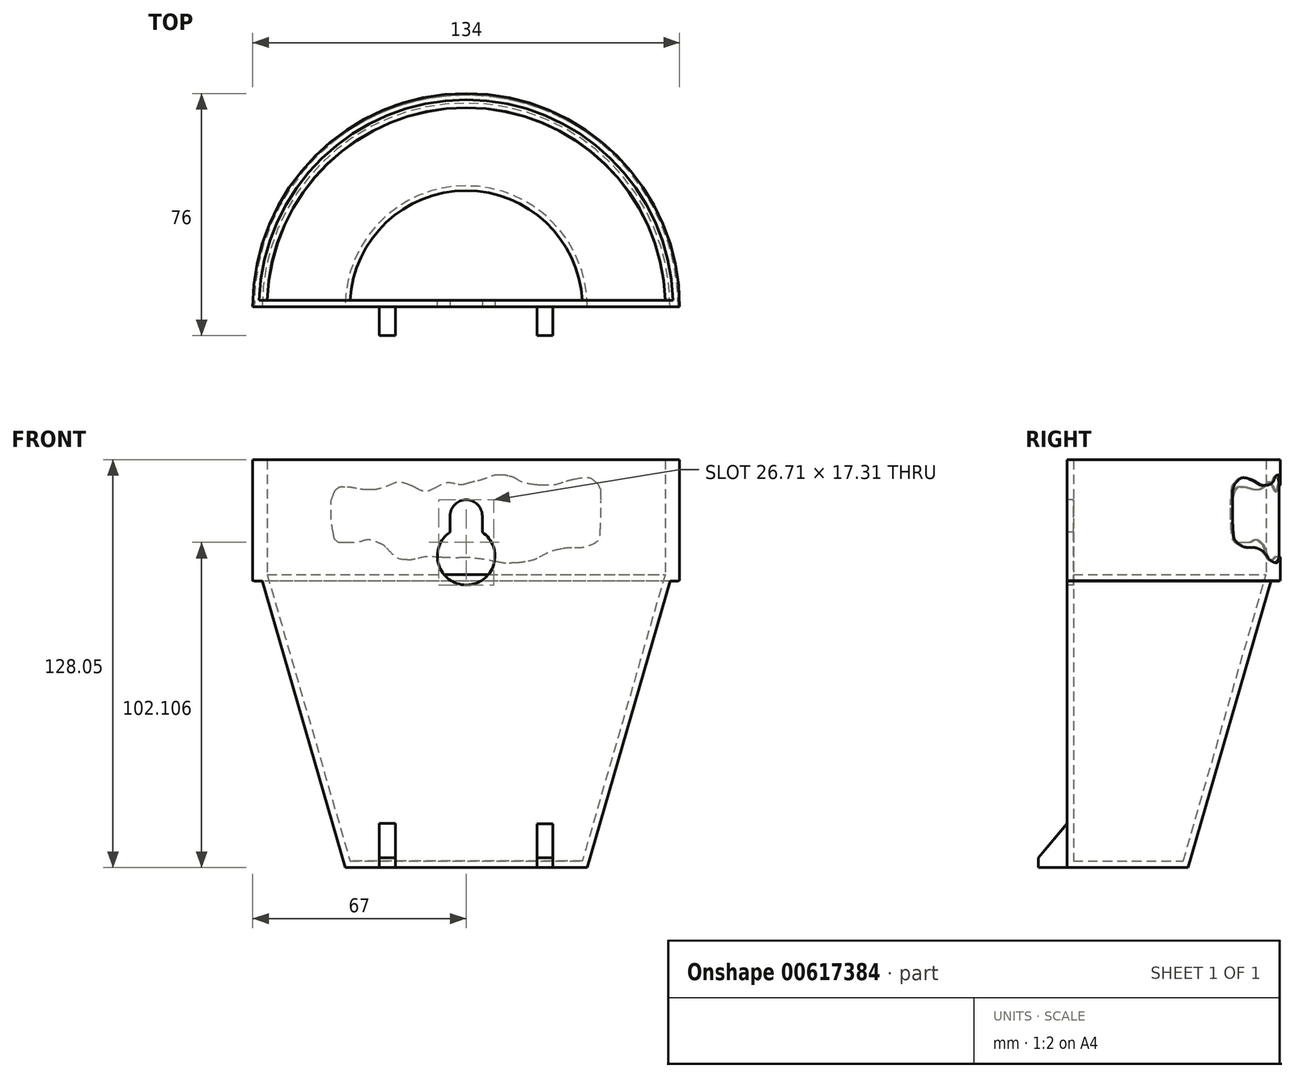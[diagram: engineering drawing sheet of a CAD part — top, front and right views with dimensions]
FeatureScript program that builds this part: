
annotation { "Feature Type Name" : "Feature", "Feature Type Description" : "" }
export const myFeature = defineFeature(function(context is Context, id is Id, definition is map)
    precondition{}
    {
        {
            var Q0;
            Q0=qCreatedBy(makeId("Front.planeOp"),FACE);
            var sketch = newSketch(context, id + "F0", { "sketchPlane" : qUnion([Q0])});
            skLineSegment(sketch, "E0", {"start": v(0, 56.42) * mm, "end": v(-67, 56.42) * mm});
            skLineSegment(sketch, "E1", {"start": v(-67, 56.42) * mm, "end": v(-67, 18.42) * mm});
            skLineSegment(sketch, "E2", {"start": v(0, -71.58) * mm, "end": v(-38, -71.58) * mm});
            skLineSegment(sketch, "E3", {"start": v(-67, 18.42) * mm, "end": v(-64, 18.42) * mm});
            skLineSegment(sketch, "E4", {"start": v(0, 56.42) * mm, "end": v(0, -71.58) * mm});
            skLineSegment(sketch, "E5", {"start": v(-64, 18.42) * mm, "end": v(-38, -71.58) * mm});
            skLineSegment(sketch, "E6.MirrorCS", {"start": v(0, 56.42) * mm, "end": v(67, 56.42) * mm});
            skLineSegment(sketch, "E7.MirrorCS", {"start": v(67, 56.42) * mm, "end": v(67, 18.42) * mm});
            skLineSegment(sketch, "E8.MirrorCS", {"start": v(67, 18.42) * mm, "end": v(64, 18.42) * mm});
            skLineSegment(sketch, "E9.MirrorCS", {"start": v(64, 18.42) * mm, "end": v(38, -71.58) * mm});
            skLineSegment(sketch, "E10.MirrorCS", {"start": v(0, -71.58) * mm, "end": v(38, -71.58) * mm});
            skSolve(sketch);
        }
        {
            var Q0;
            {var subQ0=sQuery(id+"F0.wireOp",EDGE,"E3");Q0=makeQuery(id+"F0.imprint","IMPRINT",FACE,{"disambiguationData":[TD([[makeQuery(id+"F0.imprint","IMPRINT",EDGE,{"derivedFrom":subQ0}),1.0]])]});}
            var Q1;
            {var subQ1=sQuery(id+"F0.wireOp",EDGE,"E0");Q1=makeQuery(id+"F0.imprint","IMPRINT",FACE,{"disambiguationData":[TD([[makeQuery(id+"F0.imprint","IMPRINT",EDGE,{"derivedFrom":subQ1}),1.0]])]});}
            var Q2;
            Q2=makeQuery(id+"F0.imprint","IMPRINT",FACE,{"disambiguationData":[TD([[makeQuery(id+"F0.imprint","IMPRINT",EDGE,{"derivedFrom":sQuery(id+"F0.wireOp",EDGE,"Kfnrekvc-ZjTY-c2iQ-cK4z-hKnBe4uEAVNk")}),1.0]])]});
            var Q3;
            Q3=sQuery(id+"F0.wireOp",EDGE,"E4");
            revolve(context, id + "F1", {"entities" : qUnion([Q0, Q1, Q2]), "axis" : qUnion([Q3]), "revolveType" : RevolveType.ONE_DIRECTION, "angle" : 180 * degree});
        }
        {
            var Q0;
            Q0=makeQuery(id+"FK2OT3XlAi37Aaq_1.splitOp","SPLIT",FACE,{"derivedFrom":makeQuery(id+"F1.opRevolve","SWEPT_FACE",FACE,{"disambiguationData":[OSD([sQuery(id+"F0.wireOp",EDGE,"E0")])]}),"isFromBackBody":true});
            shell(context, id + "F2", {"entities" : qUnion([Q0]), "thickness" : 2 * mm});
        }
        {
            var Q0;
            Q0=qCreatedBy(makeId("Front.planeOp"),FACE);
            var sketch = newSketch(context, id + "F3", { "sketchPlane" : qUnion([Q0])});
            skPoint(sketch, "E11.middle", {"position": v(0, -64.08) * mm});
            skLineSegment(sketch, "E12.bottom", {"start": v(-27.21, -56.57) * mm, "end": v(-22.21, -56.57) * mm});
            skLineSegment(sketch, "E12.top", {"start": v(-27.21, -71.57) * mm, "end": v(-22.21, -71.57) * mm});
            skLineSegment(sketch, "E12.left", {"start": v(-27.21, -56.57) * mm, "end": v(-27.21, -71.57) * mm});
            skLineSegment(sketch, "E12.right", {"start": v(-22.21, -56.57) * mm, "end": v(-22.21, -71.57) * mm});
            skPoint(sketch, "E12.middle", {"position": v(-24.71, -64.07) * mm});
            skLineSegment(sketch, "E13.bottom", {"start": v(22.21, -56.63) * mm, "end": v(27.21, -56.63) * mm});
            skLineSegment(sketch, "E13.top", {"start": v(22.21, -71.63) * mm, "end": v(27.21, -71.63) * mm});
            skLineSegment(sketch, "E13.left", {"start": v(22.21, -56.63) * mm, "end": v(22.21, -71.63) * mm});
            skLineSegment(sketch, "E13.right", {"start": v(27.21, -56.63) * mm, "end": v(27.21, -71.63) * mm});
            skPoint(sketch, "E13.middle", {"position": v(24.71, -64.13) * mm});
            skLineSegment(sketch, "E14", {"start": v(0, -71.68) * mm, "end": v(-22.21, -71.57) * mm, "construction": true});
            skLineSegment(sketch, "E15", {"start": v(0, -71.68) * mm, "end": v(22.21, -71.63) * mm, "construction": true});
            skSolve(sketch);
        }
        {
            var Q0;
            Q0=qSketchRegion(id+"F3",true);
            extrude(context, id + "F4", {"entities" : qUnion([Q0]), "operationType" : NewBodyOperationType.ADD, "depth" : 9 * mm});
        }
        {
            var Q0;
            Q0=qCreatedBy(makeId("Front.planeOp"),FACE);
            var sketch = newSketch(context, id + "F5", { "sketchPlane" : qUnion([Q0])});
            skCircle(sketch, "E16", {"center": v(0, 26.17) * mm, "radius": 9.05 * mm});
            skArc(sketch, "E17", {"start": v(5.05, 38.78) * mm, "mid": v(0.02, 43.83) * mm, "end": v(-5.05, 38.81) * mm});
            skLineSegment(sketch, "E18", {"start": v(-5.05, 38.81) * mm, "end": v(-5.05, 33.68) * mm});
            skLineSegment(sketch, "E19", {"start": v(5.05, 38.78) * mm, "end": v(5.05, 33.68) * mm});
            skSolve(sketch);
        }
        {
            var Q0;
            {var subQ0=sQuery(id+"F5.wireOp",EDGE,"E16");var subQ1=sQuery(id+"F5.wireOp",EDGE,"mXHq6PA0-CqQh-Lv1D-GdnR-uttjTBgCqYAd");var subQ2=makeQuery(id+"F5.imprint","INTERSECT",VERTEX,{"disambiguationData":[OD(0.0)],"derivedFrom":[subQ1,subQ0]});Q0=makeQuery(id+"F5.imprint","IMPRINT",FACE,{"disambiguationData":[TD([[makeQuery(id+"F5.imprint","IMPRINT",EDGE,{"disambiguationData":[TD([[subQ2,1.0]])],"derivedFrom":subQ1}),1.0]])]});}
            var Q1;
            {var subQ0=sQuery(id+"F5.wireOp",EDGE,"E16");var subQ1=sQuery(id+"F5.wireOp",EDGE,"mXHq6PA0-CqQh-Lv1D-GdnR-uttjTBgCqYAd");var subQ2=makeQuery(id+"F5.imprint","INTERSECT",VERTEX,{"disambiguationData":[OD(0.0)],"derivedFrom":[subQ1,subQ0]});Q1=makeQuery(id+"F5.imprint","IMPRINT",FACE,{"disambiguationData":[TD([[makeQuery(id+"F5.imprint","IMPRINT",EDGE,{"disambiguationData":[TD([[subQ2,-1.0]])],"derivedFrom":subQ1}),-1.0]])]});}
            var Q2;
            {var subQ0=sQuery(id+"F5.wireOp",EDGE,"E16");var subQ1=sQuery(id+"F5.wireOp",EDGE,"mXHq6PA0-CqQh-Lv1D-GdnR-uttjTBgCqYAd");var subQ2=makeQuery(id+"F5.imprint","INTERSECT",VERTEX,{"disambiguationData":[OD(0.0)],"derivedFrom":[subQ1,subQ0]});Q2=makeQuery(id+"F5.imprint","IMPRINT",FACE,{"disambiguationData":[TD([[makeQuery(id+"F5.imprint","IMPRINT",EDGE,{"disambiguationData":[TD([[subQ2,-1.0]])],"derivedFrom":subQ1}),1.0]])]});}
            var Q3;
            Q3=makeQuery(id+"F5.imprint","IMPRINT",FACE,{"disambiguationData":[TD([[makeQuery(id+"F5.imprint","IMPRINT",EDGE,{"derivedFrom":sQuery(id+"F5.wireOp",EDGE,"E17")}),1.0]])]});
            var Q4;
            {var subQ0=sQuery(id+"F5.wireOp",EDGE,"E16");var subQ1=makeQuery(id+"F5.imprint","INTERSECT",VERTEX,{"derivedFrom":[subQ0,sQuery(id+"F5.wireOp",EDGE,"E18")]});Q4=makeQuery(id+"F5.imprint","IMPRINT",FACE,{"disambiguationData":[TD([[makeQuery(id+"F5.imprint","IMPRINT",EDGE,{"disambiguationData":[TD([[subQ1,1.0]])],"derivedFrom":subQ0}),1.0]])]});}
            var Q5;
            Q5=sQuery(id+"F5.wireOp",EDGE,"mXHq6PA0-CqQh-Lv1D-GdnR-uttjTBgCqYAd");
            var Q6;
            Q6=sQuery(id+"F5.wireOp",EDGE,"E16");
            extrude(context, id + "F6", {"entities" : qUnion([Q0, Q1, Q2, Q3, Q4]), "operationType" : NewBodyOperationType.REMOVE, "surfaceEntities" : qUnion([Q5, Q6]), "oppositeDirection" : true, "depth" : 10 * mm, "offsetDistance" : 25 * mm});
        }
        {
            var Q0;
            Q0=makeQuery(id+"F4.opExtrude","CAP_EDGE",EDGE,{"disambiguationData":[OSD([sQuery(id+"F3.wireOp",EDGE,"E11.bottom")])],"isStart":false});
            var Q1;
            Q1=makeQuery(id+"F4.opExtrude","CAP_EDGE",EDGE,{"disambiguationData":[OSD([sQuery(id+"F3.wireOp",EDGE,"E12.bottom")])],"isStart":false});
            var Q2;
            Q2=makeQuery(id+"F4.opExtrude","CAP_EDGE",EDGE,{"disambiguationData":[OSD([sQuery(id+"F3.wireOp",EDGE,"E13.bottom")])],"isStart":false});
            chamfer(context, id + "F7", {"entities" : qUnion([Q0, Q1, Q2]), "chamferType" : ChamferType.OFFSET_ANGLE, "width" : 10 * mm, "oppositeDirection" : false, "angle" : 50 * degree, "tangentPropagation" : true});
        }
        {
            var Q0;
            Q0=makeQuery(id+"F2.opShell","OFFSET_FACE",FACE,{"disambiguationData":[OSD([sQuery(id+"F0.wireOp",EDGE,"E0"),sQuery(id+"F0.wireOp",EDGE,"E1"),sQuery(id+"F0.wireOp",EDGE,"E2"),sQuery(id+"F0.wireOp",EDGE,"E3"),sQuery(id+"F0.wireOp",EDGE,"E4"),sQuery(id+"F0.wireOp",EDGE,"E5")])]});
            cPlane(context, id + "F8", {"entities" : qUnion([Q0]), "cplaneType" : CPlaneType.OFFSET, "offset" : 66.8 * mm, "width" : 150 * mm, "height" : 150 * mm});
        }
        {
            var Q0;
            Q0=makeQuery(id+"F1.opRevolve","SWEPT_FACE",FACE,{"disambiguationData":[OSD([sQuery(id+"F0.wireOp",EDGE,"E0")])]});
            var sketch = newSketch(context, id + "F9", { "sketchPlane" : qUnion([Q0])});
            skCircle(sketch, "E20", {"center": v(0, 0) * mm, "radius": 67.75 * mm});
            skCircle(sketch, "E21", {"center": v(0, 0) * mm, "radius": 91 * mm});
            skSolve(sketch);
        }
        {
            var Q0;
            Q0=qSketchRegion(id+"F9",true);
            extrude(context, id + "F10", {"entities" : qUnion([Q0]), "operationType" : NewBodyOperationType.REMOVE, "oppositeDirection" : true, "depth" : 124 * mm});
        }
        {
            var Q0;
            Q0=qCreatedBy(id+"F8.planeOp",FACE);
            var sketch = newSketch(context, id + "F11", { "sketchPlane" : qUnion([Q0])});
            skFitSpline(sketch, "E22", {"points": [v(-14.21, 60.71) * mm, v(-15.23, 60.8) * mm, v(-17.15, 61.07) * mm, v(-17.98, 61.24) * mm]});
            skFitSpline(sketch, "E23", {"points": [v(-17.98, 61.24) * mm, v(-19.27, 61.5) * mm, v(-20.2, 61.84) * mm, v(-21.41, 62.47) * mm]});
            skFitSpline(sketch, "E24", {"points": [v(-21.41, 62.47) * mm, v(-24.2, 63.93) * mm, v(-26.13, 64.66) * mm, v(-28.48, 65.15) * mm]});
            skFitSpline(sketch, "E25", {"points": [v(-28.48, 65.15) * mm, v(-29.29, 65.32) * mm, v(-30, 65.37) * mm, v(-32.2, 65.43) * mm]});
            skFitSpline(sketch, "E26", {"points": [v(-32.2, 65.43) * mm, v(-35.22, 65.52) * mm, v(-35.76, 65.6) * mm, v(-36.93, 66.16) * mm]});
            skFitSpline(sketch, "E27", {"points": [v(-36.93, 66.16) * mm, v(-38.77, 67.04) * mm, v(-39.83, 68.44) * mm, v(-40.02, 70.25) * mm]});
            skFitSpline(sketch, "E28", {"points": [v(-40.02, 70.25) * mm, v(-40.16, 71.57) * mm, v(-40.28, 76.7) * mm, v(-40.26, 80.14) * mm]});
            skFitSpline(sketch, "E29", {"points": [v(-39.96, 84.14) * mm, v(-39.6, 85.02) * mm, v(-39.23, 85.55) * mm, v(-38.6, 86.04) * mm]});
            skFitSpline(sketch, "E30", {"points": [v(-38.6, 86.04) * mm, v(-37.32, 87.06) * mm, v(-35.24, 87.34) * mm, v(-32.5, 86.87) * mm]});
            skFitSpline(sketch, "E31", {"points": [v(-32.5, 86.87) * mm, v(-31.47, 86.7) * mm, v(-30.34, 86.4) * mm, v(-28.67, 85.86) * mm]});
            skFitSpline(sketch, "E32", {"points": [v(-28.67, 85.86) * mm, v(-26.48, 85.16) * mm, v(-25.24, 84.96) * mm, v(-23.15, 84.96) * mm]});
            skFitSpline(sketch, "E33", {"points": [v(-23.15, 84.96) * mm, v(-22.35, 84.96) * mm, v(-21.18, 85.03) * mm, v(-20.54, 85.12) * mm]});
            skFitSpline(sketch, "E34", {"points": [v(-20.54, 85.12) * mm, v(-18.34, 85.42) * mm, v(-15.77, 86.13) * mm, v(-14.88, 86.67) * mm]});
            skFitSpline(sketch, "E35", {"points": [v(-14.88, 86.67) * mm, v(-14.07, 87.17) * mm, v(-12.87, 87.67) * mm, v(-11.9, 87.91) * mm]});
            skFitSpline(sketch, "E36", {"points": [v(-11.9, 87.91) * mm, v(-11.18, 88.1) * mm, v(-10.77, 88.13) * mm, v(-9.58, 88.13) * mm]});
            skFitSpline(sketch, "E37", {"points": [v(-9.58, 88.13) * mm, v(-7.91, 88.13) * mm, v(-7.18, 87.99) * mm, v(-5.29, 87.27) * mm]});
            skFitSpline(sketch, "E38", {"points": [v(-5.29, 87.27) * mm, v(-3.99, 86.78) * mm, v(-2.9, 86.45) * mm, v(-1.6, 86.14) * mm]});
            skFitSpline(sketch, "E39", {"points": [v(-1.6, 86.14) * mm, v(-1.1, 86.03) * mm, v(-0.13, 85.78) * mm, v(0.55, 85.59) * mm]});
            skFitSpline(sketch, "E40", {"points": [v(0.55, 85.59) * mm, v(2.03, 85.17) * mm, v(2.79, 85.14) * mm, v(4.3, 85.4) * mm]});
            skFitSpline(sketch, "E41", {"points": [v(4.3, 85.4) * mm, v(6.34, 85.76) * mm, v(7.65, 85.52) * mm, v(10.1, 84.34) * mm]});
            skFitSpline(sketch, "E42", {"points": [v(10.1, 84.34) * mm, v(12.42, 83.22) * mm, v(13.55, 82.94) * mm, v(14.56, 83.25) * mm]});
            skFitSpline(sketch, "E43", {"points": [v(14.56, 83.25) * mm, v(14.85, 83.34) * mm, v(15.6, 83.69) * mm, v(16.21, 84.03) * mm]});
            skFitSpline(sketch, "E44", {"points": [v(16.21, 84.03) * mm, v(16.83, 84.37) * mm, v(17.63, 84.77) * mm, v(17.97, 84.9) * mm]});
            skFitSpline(sketch, "E45", {"points": [v(17.97, 84.9) * mm, v(19, 85.32) * mm, v(21.27, 85.96) * mm, v(22.8, 85.75) * mm]});
            skFitSpline(sketch, "E46", {"points": [v(22.8, 85.75) * mm, v(25.09, 84.74) * mm, v(26.57, 84.16) * mm, v(27.89, 83.82) * mm]});
            skFitSpline(sketch, "E47", {"points": [v(27.89, 83.82) * mm, v(28.82, 83.6) * mm, v(29.1, 83.56) * mm, v(30.58, 83.57) * mm]});
            skFitSpline(sketch, "E48", {"points": [v(30.58, 83.57) * mm, v(32.1, 83.57) * mm, v(32.41, 83.6) * mm, v(34.6, 84) * mm]});
            skFitSpline(sketch, "E49", {"points": [v(34.6, 84) * mm, v(36.58, 84.35) * mm, v(37.14, 84.42) * mm, v(38.19, 84.42) * mm]});
            skFitSpline(sketch, "E50", {"points": [v(38.19, 84.42) * mm, v(39.58, 84.42) * mm, v(39.98, 84.31) * mm, v(40.62, 83.8) * mm]});
            skFitSpline(sketch, "E51", {"points": [v(40.62, 83.8) * mm, v(41.14, 83.38) * mm, v(41.5, 82.8) * mm, v(41.88, 81.74) * mm]});
            skFitSpline(sketch, "E52", {"points": [v(41.88, 81.74) * mm, v(42.44, 80.2) * mm, v(42.49, 79.85) * mm, v(42.49, 77.2) * mm]});
            skFitSpline(sketch, "E53", {"points": [v(42.49, 77.2) * mm, v(42.48, 74.69) * mm, v(42.34, 72.96) * mm, v(41.92, 70.56) * mm]});
            skFitSpline(sketch, "E54", {"points": [v(41.92, 70.56) * mm, v(41.56, 68.48) * mm, v(41.46, 68.19) * mm, v(40.86, 67.68) * mm]});
            skFitSpline(sketch, "E55", {"points": [v(40.86, 67.68) * mm, v(40.27, 67.18) * mm, v(39.77, 67.05) * mm, v(38.23, 67.05) * mm]});
            skFitSpline(sketch, "E56", {"points": [v(38.23, 67.05) * mm, v(35.56, 67.04) * mm, v(34.05, 67.16) * mm, v(33.1, 67.44) * mm]});
            skFitSpline(sketch, "E57", {"points": [v(33.1, 67.44) * mm, v(31.4, 67.95) * mm, v(30.14, 67.86) * mm, v(28.22, 67.1) * mm]});
            skFitSpline(sketch, "E58", {"points": [v(28.22, 67.1) * mm, v(26.75, 66.51) * mm, v(26.28, 66.21) * mm, v(25.37, 65.28) * mm]});
            skFitSpline(sketch, "E59", {"points": [v(25.37, 65.28) * mm, v(23.19, 63.06) * mm, v(21.33, 61.94) * mm, v(19.52, 61.74) * mm]});
            skFitSpline(sketch, "E60", {"points": [v(19.52, 61.74) * mm, v(18.5, 61.63) * mm, v(17.41, 61.74) * mm, v(15.77, 62.11) * mm]});
            skFitSpline(sketch, "E61", {"points": [v(15.77, 62.11) * mm, v(13.66, 62.6) * mm, v(12.37, 62.66) * mm, v(8.71, 62.47) * mm]});
            skFitSpline(sketch, "E62", {"points": [v(8.71, 62.47) * mm, v(6.82, 62.37) * mm, v(4.44, 62.32) * mm, v(2.66, 62.33) * mm]});
            skFitSpline(sketch, "E63", {"points": [v(2.66, 62.33) * mm, v(0.28, 62.35) * mm, v(-0.53, 62.32) * mm, v(-1.6, 62.18) * mm]});
            skFitSpline(sketch, "E64", {"points": [v(-1.6, 62.18) * mm, v(-3.69, 61.9) * mm, v(-5.8, 61.56) * mm, v(-8.26, 61.08) * mm]});
            skFitSpline(sketch, "E65", {"points": [v(-8.26, 61.08) * mm, v(-10.46, 60.66) * mm, v(-10.6, 60.65) * mm, v(-12.2, 60.67) * mm]});
            skFitSpline(sketch, "E66", {"points": [v(-12.2, 60.67) * mm, v(-13.1, 60.68) * mm, v(-14, 60.7) * mm, v(-14.21, 60.71) * mm]});
            skLineSegment(sketch, "E67", {"start": v(-40.26, 80.14) * mm, "end": v(-40.23, 83.46) * mm});
            skLineSegment(sketch, "E68", {"start": v(-40.23, 83.46) * mm, "end": v(-39.96, 84.14) * mm});
            skLineSegment(sketch, "E69", {"start": v(-39.96, 84.14) * mm, "end": v(-40.26, 80.14) * mm});
            skFitSpline(sketch, "E70", {"points": [v(-15.59, 24.15) * mm, v(-16.63, 24.24) * mm, v(-18.6, 24.5) * mm, v(-19.44, 24.68) * mm]});
            skFitSpline(sketch, "E71", {"points": [v(-19.44, 24.68) * mm, v(-20.76, 24.94) * mm, v(-21.72, 25.28) * mm, v(-22.96, 25.91) * mm]});
            skFitSpline(sketch, "E72", {"points": [v(-22.96, 25.91) * mm, v(-25.81, 27.37) * mm, v(-27.79, 28.1) * mm, v(-30.2, 28.6) * mm]});
            skFitSpline(sketch, "E73", {"points": [v(-30.2, 28.6) * mm, v(-31.02, 28.76) * mm, v(-31.76, 28.81) * mm, v(-34.01, 28.87) * mm]});
            skFitSpline(sketch, "E74", {"points": [v(-34.01, 28.87) * mm, v(-37.1, 28.96) * mm, v(-37.65, 29.04) * mm, v(-38.85, 29.6) * mm]});
            skFitSpline(sketch, "E75", {"points": [v(-38.85, 29.6) * mm, v(-40.73, 30.48) * mm, v(-41.82, 31.88) * mm, v(-42.02, 33.69) * mm]});
            skFitSpline(sketch, "E76", {"points": [v(-42.02, 33.69) * mm, v(-42.16, 35) * mm, v(-42.29, 40.13) * mm, v(-42.26, 43.57) * mm]});
            skFitSpline(sketch, "E77", {"points": [v(-41.95, 47.57) * mm, v(-41.59, 48.46) * mm, v(-41.2, 48.98) * mm, v(-40.57, 49.47) * mm]});
            skFitSpline(sketch, "E78", {"points": [v(-40.57, 49.47) * mm, v(-39.25, 50.5) * mm, v(-37.12, 50.77) * mm, v(-34.3, 50.3) * mm]});
            skFitSpline(sketch, "E79", {"points": [v(-34.3, 50.3) * mm, v(-33.26, 50.13) * mm, v(-32.1, 49.83) * mm, v(-30.4, 49.3) * mm]});
            skFitSpline(sketch, "E80", {"points": [v(-30.4, 49.3) * mm, v(-28.15, 48.6) * mm, v(-26.88, 48.4) * mm, v(-24.74, 48.4) * mm]});
            skFitSpline(sketch, "E81", {"points": [v(-24.74, 48.4) * mm, v(-23.91, 48.4) * mm, v(-22.72, 48.47) * mm, v(-22.06, 48.56) * mm]});
            skFitSpline(sketch, "E82", {"points": [v(-22.06, 48.56) * mm, v(-19.81, 48.86) * mm, v(-17.18, 49.56) * mm, v(-16.26, 50.1) * mm]});
            skFitSpline(sketch, "E83", {"points": [v(-16.26, 50.1) * mm, v(-15.44, 50.6) * mm, v(-14.2, 51.1) * mm, v(-13.21, 51.35) * mm]});
            skFitSpline(sketch, "E84", {"points": [v(-13.21, 51.35) * mm, v(-12.48, 51.53) * mm, v(-12.06, 51.57) * mm, v(-10.84, 51.57) * mm]});
            skFitSpline(sketch, "E85", {"points": [v(-10.84, 51.57) * mm, v(-9.13, 51.57) * mm, v(-8.38, 51.42) * mm, v(-6.44, 50.7) * mm]});
            skFitSpline(sketch, "E86", {"points": [v(-6.44, 50.7) * mm, v(-5.11, 50.21) * mm, v(-4, 49.88) * mm, v(-2.67, 49.58) * mm]});
            skFitSpline(sketch, "E87", {"points": [v(-2.67, 49.58) * mm, v(-2.15, 49.46) * mm, v(-1.16, 49.21) * mm, v(-0.46, 49.02) * mm]});
            skFitSpline(sketch, "E88", {"points": [v(-0.46, 49.02) * mm, v(1.05, 48.61) * mm, v(1.82, 48.57) * mm, v(3.38, 48.84) * mm]});
            skFitSpline(sketch, "E89", {"points": [v(3.38, 48.84) * mm, v(5.46, 49.2) * mm, v(6.8, 48.96) * mm, v(9.3, 47.78) * mm]});
            skFitSpline(sketch, "E90", {"points": [v(9.3, 47.78) * mm, v(11.69, 46.66) * mm, v(12.85, 46.38) * mm, v(13.88, 46.69) * mm]});
            skFitSpline(sketch, "E91", {"points": [v(13.88, 46.69) * mm, v(14.18, 46.77) * mm, v(14.94, 47.12) * mm, v(15.57, 47.47) * mm]});
            skFitSpline(sketch, "E92", {"points": [v(15.57, 47.47) * mm, v(16.21, 47.8) * mm, v(17.02, 48.2) * mm, v(17.38, 48.34) * mm]});
            skFitSpline(sketch, "E93", {"points": [v(17.38, 48.34) * mm, v(18.43, 48.76) * mm, v(20.75, 49.4) * mm, v(22.33, 49.19) * mm]});
            skFitSpline(sketch, "E94", {"points": [v(22.33, 49.19) * mm, v(24.66, 48.17) * mm, v(26.18, 47.6) * mm, v(27.53, 47.26) * mm]});
            skFitSpline(sketch, "E95", {"points": [v(27.53, 47.26) * mm, v(28.48, 47.03) * mm, v(28.77, 47) * mm, v(30.29, 47) * mm]});
            skFitSpline(sketch, "E96", {"points": [v(30.29, 47) * mm, v(31.85, 47) * mm, v(32.17, 47.04) * mm, v(34.4, 47.43) * mm]});
            skFitSpline(sketch, "E97", {"points": [v(34.4, 47.43) * mm, v(36.44, 47.79) * mm, v(37, 47.85) * mm, v(38.08, 47.85) * mm]});
            skFitSpline(sketch, "E98", {"points": [v(38.08, 47.85) * mm, v(39.5, 47.85) * mm, v(39.91, 47.75) * mm, v(40.57, 47.23) * mm]});
            skFitSpline(sketch, "E99", {"points": [v(40.57, 47.23) * mm, v(41.1, 46.81) * mm, v(41.47, 46.23) * mm, v(41.86, 45.17) * mm]});
            skFitSpline(sketch, "E100", {"points": [v(41.86, 45.17) * mm, v(42.44, 43.64) * mm, v(42.49, 43.29) * mm, v(42.48, 40.64) * mm]});
            skFitSpline(sketch, "E101", {"points": [v(42.48, 40.64) * mm, v(42.48, 38.12) * mm, v(42.33, 36.4) * mm, v(41.9, 34) * mm]});
            skFitSpline(sketch, "E102", {"points": [v(41.9, 34) * mm, v(41.54, 31.92) * mm, v(41.43, 31.63) * mm, v(40.82, 31.12) * mm]});
            skFitSpline(sketch, "E103", {"points": [v(40.82, 31.12) * mm, v(40.22, 30.61) * mm, v(39.7, 30.5) * mm, v(38.12, 30.49) * mm]});
            skFitSpline(sketch, "E104", {"points": [v(38.12, 30.49) * mm, v(35.4, 30.48) * mm, v(33.85, 30.6) * mm, v(32.87, 30.88) * mm]});
            skFitSpline(sketch, "E105", {"points": [v(32.87, 30.88) * mm, v(31.13, 31.39) * mm, v(29.84, 31.3) * mm, v(27.87, 30.53) * mm]});
            skFitSpline(sketch, "E106", {"points": [v(27.87, 30.53) * mm, v(26.37, 29.95) * mm, v(25.89, 29.65) * mm, v(24.95, 28.72) * mm]});
            skFitSpline(sketch, "E107", {"points": [v(24.95, 28.72) * mm, v(22.72, 26.5) * mm, v(20.82, 25.38) * mm, v(18.96, 25.18) * mm]});
            skFitSpline(sketch, "E108", {"points": [v(18.96, 25.18) * mm, v(17.91, 25.07) * mm, v(16.8, 25.18) * mm, v(15.12, 25.55) * mm]});
            skFitSpline(sketch, "E109", {"points": [v(15.12, 25.55) * mm, v(12.96, 26.03) * mm, v(11.64, 26.1) * mm, v(7.9, 25.9) * mm]});
            skFitSpline(sketch, "E110", {"points": [v(7.9, 25.9) * mm, v(5.96, 25.8) * mm, v(3.52, 25.75) * mm, v(1.7, 25.77) * mm]});
            skFitSpline(sketch, "E111", {"points": [v(1.7, 25.77) * mm, v(-0.74, 25.79) * mm, v(-1.57, 25.76) * mm, v(-2.67, 25.62) * mm]});
            skFitSpline(sketch, "E112", {"points": [v(-2.67, 25.62) * mm, v(-4.8, 25.34) * mm, v(-6.97, 25) * mm, v(-9.5, 24.52) * mm]});
            skFitSpline(sketch, "E113", {"points": [v(-9.5, 24.52) * mm, v(-11.74, 24.1) * mm, v(-11.88, 24.09) * mm, v(-13.52, 24.1) * mm]});
            skFitSpline(sketch, "E114", {"points": [v(-13.52, 24.1) * mm, v(-14.45, 24.11) * mm, v(-15.38, 24.14) * mm, v(-15.59, 24.15) * mm]});
            skLineSegment(sketch, "E115", {"start": v(-42.26, 43.57) * mm, "end": v(-42.23, 46.9) * mm});
            skLineSegment(sketch, "E116", {"start": v(-42.23, 46.9) * mm, "end": v(-41.95, 47.57) * mm});
            skLineSegment(sketch, "E117", {"start": v(-41.95, 47.57) * mm, "end": v(-42.26, 43.57) * mm});
            skSolve(sketch);
        }
        {
            var Q0;
            Q0=qSketchRegion(id+"F11",true);
            extrude(context, id + "F12", {"entities" : qUnion([Q0]), "operationType" : NewBodyOperationType.REMOVE, "oppositeDirection" : true, "depth" : 30 * mm, "offsetDistance" : 25 * mm});
        }
        {
            var Q0;
            Q0=qCreatedBy(makeId("Front.planeOp"),FACE);
            var sketch = newSketch(context, id + "F13", { "sketchPlane" : qUnion([Q0])});
            skLineSegment(sketch, "E118.bottom", {"start": v(66.54, 56.4) * mm, "end": v(62.54, 56.4) * mm});
            skLineSegment(sketch, "E118.top", {"start": v(66.54, 18.4) * mm, "end": v(62.54, 18.4) * mm});
            skLineSegment(sketch, "E118.left", {"start": v(66.54, 56.4) * mm, "end": v(66.54, 18.4) * mm});
            skLineSegment(sketch, "E118.right", {"start": v(62.54, 56.4) * mm, "end": v(62.54, 18.4) * mm});
            skSolve(sketch);
        }
        {
            var Q0;
            Q0=qSketchRegion(id+"F13",true);
            var Q1;
            Q1=sQuery(id+"F0.wireOp",EDGE,"E4");
            revolve(context, id + "F14", {"operationType" : NewBodyOperationType.ADD, "entities" : qUnion([Q0]), "axis" : qUnion([Q1]), "revolveType" : RevolveType.ONE_DIRECTION, "oppositeDirection" : true, "angle" : 180 * degree});
        }
    });
